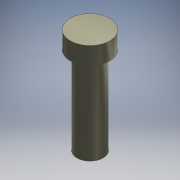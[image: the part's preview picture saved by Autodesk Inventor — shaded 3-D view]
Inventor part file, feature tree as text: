
AUTODESK INVENTOR PART (.ipt)
format: ipt  version: 2016 (Build 200138000, 138)  size: 97,280 bytes
history: native  units: mm
features: extrude x2, other x1, sketch x1
ambient origin geometry x8: Origin, YZ Plane, XZ Plane, XY Plane, X Axis, Y Axis, Z Axis, Center Point
bodies: Body1 (feature_tree)
feature tree (4):
  other  "ソリッド1"
  sketch  "スケッチ1"
  extrude  "押し出し1"  Depth=4.5mm
  extrude  "押し出し2"  Depth=3.0mm
